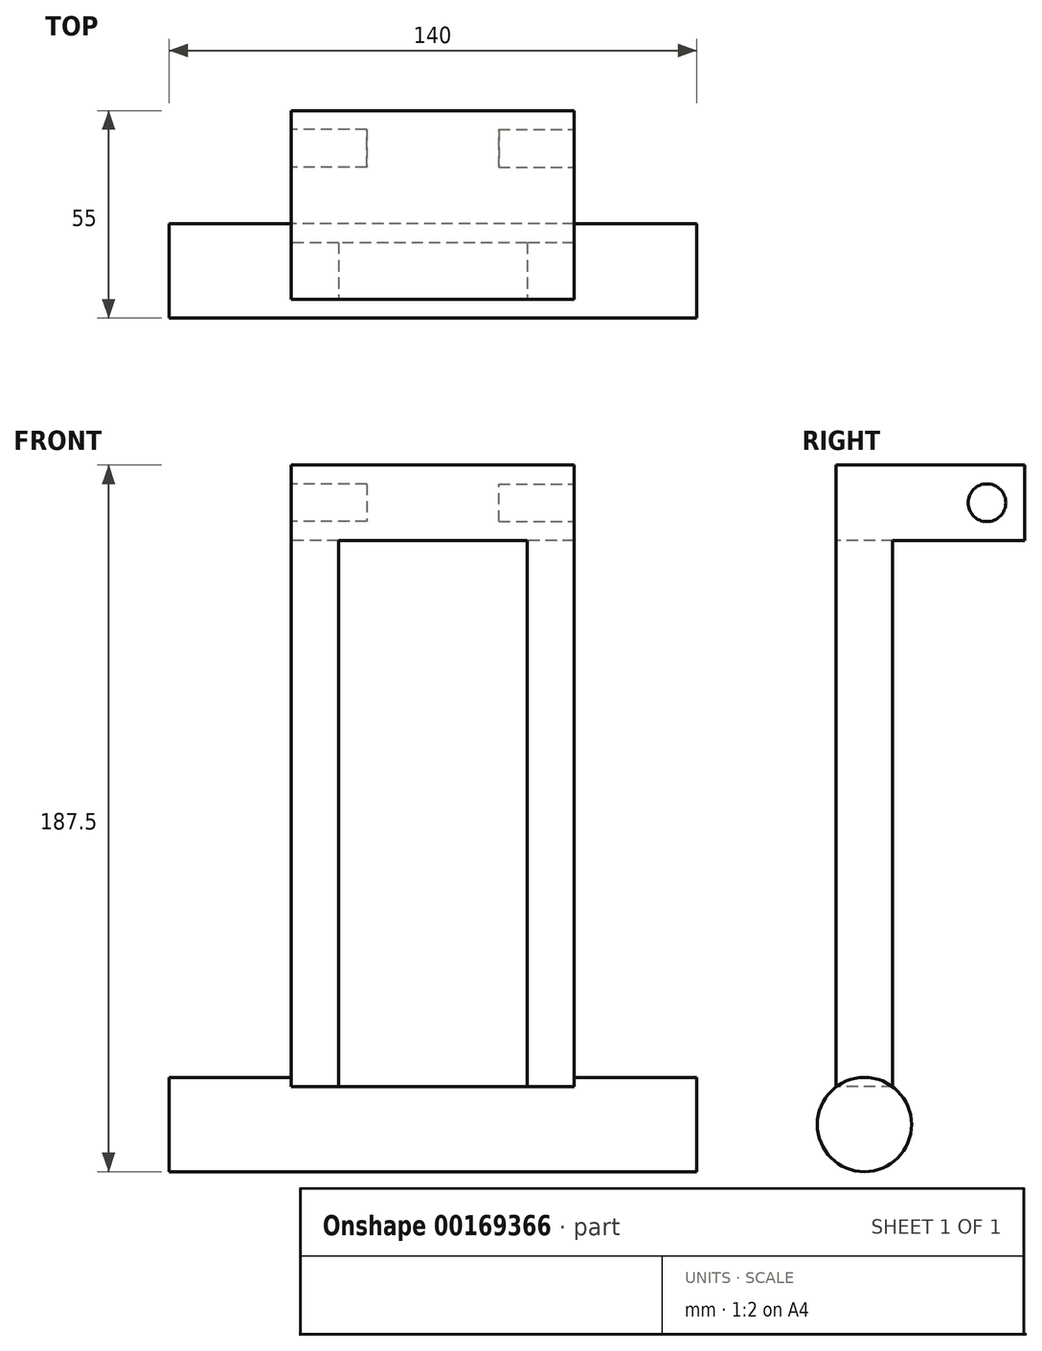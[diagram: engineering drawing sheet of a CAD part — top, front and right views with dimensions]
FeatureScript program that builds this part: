
annotation { "Feature Type Name" : "Feature", "Feature Type Description" : "" }
export const myFeature = defineFeature(function(context is Context, id is Id, definition is map)
    precondition{}
    {
        {
            var Q0;
            Q0=qCreatedBy(makeId("Right.planeOp"),FACE);
            var sketch = newSketch(context, id + "F0", { "sketchPlane" : qUnion([Q0])});
            skCircle(sketch, "E0", {"center": v(0, 0) * mm, "radius": 12.5 * mm});
            skSolve(sketch);
        }
        {
            var Q0;
            Q0=makeQuery(id+"F0.imprint","IMPRINT",FACE,{"disambiguationData":[TD([[makeQuery(id+"F0.imprint","IMPRINT",EDGE,{"derivedFrom":sQuery(id+"F0.wireOp",EDGE,"E0")}),1.0]])]});
            extrude(context, id + "F1", {"entities" : qUnion([Q0]), "endBound" : BoundingType.SYMMETRIC, "depth" : 140 * mm});
        }
        {
            var Q0;
            Q0=qCreatedBy(makeId("Top.planeOp"),FACE);
            var sketch = newSketch(context, id + "F2", { "sketchPlane" : qUnion([Q0])});
            skLineSegment(sketch, "E1.bottom", {"start": v(37.5, 7.5) * mm, "end": v(-37.5, 7.5) * mm});
            skLineSegment(sketch, "E1.top", {"start": v(37.5, -7.5) * mm, "end": v(-37.5, -7.5) * mm});
            skLineSegment(sketch, "E1.left", {"start": v(37.5, 7.5) * mm, "end": v(37.5, -7.5) * mm});
            skLineSegment(sketch, "E1.right", {"start": v(-37.5, 7.5) * mm, "end": v(-37.5, -7.5) * mm});
            skPoint(sketch, "E1.middle", {"position": v(0, 0) * mm});
            skSolve(sketch);
        }
        {
            var Q0;
            Q0=qSketchRegion(id+"F2",true);
            extrude(context, id + "F3", {"entities" : qUnion([Q0]), "operationType" : NewBodyOperationType.ADD, "depth" : 175 * mm});
        }
        {
            var Q0;
            Q0=makeQuery(id+"F3.opExtrude","SWEPT_FACE",FACE,{"disambiguationData":[OSD([sQuery(id+"F2.wireOp",EDGE,"E1.top")])]});
            var sketch = newSketch(context, id + "F4", { "sketchPlane" : qUnion([Q0])});
            skLineSegment(sketch, "E2.bottom", {"start": v(0, 10) * mm, "end": v(25, 10) * mm});
            skLineSegment(sketch, "E2.top", {"start": v(0, 155) * mm, "end": v(25, 155) * mm});
            skLineSegment(sketch, "E2.left", {"start": v(0, 10) * mm, "end": v(0, 155) * mm});
            skLineSegment(sketch, "E2.right", {"start": v(25, 10) * mm, "end": v(25, 155) * mm});
            skLineSegment(sketch, "E3.MirrorCS", {"start": v(0, 155) * mm, "end": v(-25, 155) * mm});
            skLineSegment(sketch, "E4.MirrorCS", {"start": v(-25, 10) * mm, "end": v(-25, 155) * mm});
            skLineSegment(sketch, "E5.MirrorCS", {"start": v(0, 10) * mm, "end": v(-25, 10) * mm});
            skSolve(sketch);
        }
        {
            var Q0;
            Q0=makeQuery(id+"F4.imprint","IMPRINT",FACE,{"disambiguationData":[TD([[makeQuery(id+"F4.imprint","IMPRINT",EDGE,{"derivedFrom":sQuery(id+"F4.wireOp",EDGE,"E2.left")}),1.0]])]});
            var Q1;
            Q1=makeQuery(id+"F4.imprint","IMPRINT",FACE,{"disambiguationData":[TD([[makeQuery(id+"F4.imprint","IMPRINT",EDGE,{"derivedFrom":sQuery(id+"F4.wireOp",EDGE,"E2.bottom")}),-1.0]])]});
            extrude(context, id + "F5", {"entities" : qUnion([Q0, Q1]), "operationType" : NewBodyOperationType.REMOVE, "oppositeDirection" : true, "depth" : 500 * mm});
        }
        {
            var Q0;
            Q0=makeQuery(id+"F3.opExtrude","SWEPT_FACE",FACE,{"disambiguationData":[OSD([sQuery(id+"F2.wireOp",EDGE,"E1.top")])]});
            var sketch = newSketch(context, id + "F6", { "sketchPlane" : qUnion([Q0])});
            skPoint(sketch, "E6.oppositeSnap0", {"position": v(0, 155) * mm});
            skLineSegment(sketch, "E6.bottom", {"start": v(-37.5, 175) * mm, "end": v(37.5, 175) * mm});
            skLineSegment(sketch, "E6.top", {"start": v(-37.5, 155) * mm, "end": v(37.5, 155) * mm});
            skLineSegment(sketch, "E6.left", {"start": v(-37.5, 175) * mm, "end": v(-37.5, 155) * mm});
            skLineSegment(sketch, "E6.right", {"start": v(37.5, 175) * mm, "end": v(37.5, 155) * mm});
            skSolve(sketch);
        }
        {
            var Q0;
            Q0=qSketchRegion(id+"F6",true);
            extrude(context, id + "F7", {"entities" : qUnion([Q0]), "operationType" : NewBodyOperationType.ADD, "oppositeDirection" : true, "depth" : 50 * mm});
        }
        {
            var Q0;
            Q0=makeQuery(id+"F7.boolean.opBoolean","MERGE",FACE,{"derivedFrom":[makeQuery(id+"F3.opExtrude","SWEPT_FACE",FACE,{"disambiguationData":[OSD([sQuery(id+"F2.wireOp",EDGE,"E1.right")])]}),makeQuery(id+"F7.opExtrude","SWEPT_FACE",FACE,{"disambiguationData":[OSD([sQuery(id+"F6.wireOp",EDGE,"E6.left")])]})]});
            var sketch = newSketch(context, id + "F8", { "sketchPlane" : qUnion([Q0])});
            skPoint(sketch, "E7", {"position": v(-42.5, 165) * mm});
            skCircle(sketch, "E8", {"center": v(-32.5, 165) * mm, "radius": 5 * mm});
            skSolve(sketch);
        }
        {
            var Q0;
            Q0=makeQuery(id+"F8.imprint","IMPRINT",FACE,{"disambiguationData":[TD([[makeQuery(id+"F8.imprint","IMPRINT",EDGE,{"derivedFrom":sQuery(id+"F8.wireOp",EDGE,"E8")}),1.0]])]});
            extrude(context, id + "F9", {"entities" : qUnion([Q0]), "operationType" : NewBodyOperationType.REMOVE, "oppositeDirection" : true, "depth" : 20 * mm});
        }
        {
            var Q0;
            Q0=makeQuery(id+"F7.boolean.opBoolean","MERGE",FACE,{"derivedFrom":[makeQuery(id+"F3.opExtrude","SWEPT_FACE",FACE,{"disambiguationData":[OSD([sQuery(id+"F2.wireOp",EDGE,"E1.left")])]}),makeQuery(id+"F7.opExtrude","SWEPT_FACE",FACE,{"disambiguationData":[OSD([sQuery(id+"F6.wireOp",EDGE,"E6.right")])]})]});
            var sketch = newSketch(context, id + "F10", { "sketchPlane" : qUnion([Q0])});
            skPoint(sketch, "E9", {"position": v(42.5, 165) * mm});
            skCircle(sketch, "E10", {"center": v(32.5, 165) * mm, "radius": 5 * mm});
            skSolve(sketch);
        }
        {
            var Q0;
            Q0=qSketchRegion(id+"F10",true);
            extrude(context, id + "F11", {"entities" : qUnion([Q0]), "operationType" : NewBodyOperationType.REMOVE, "oppositeDirection" : true, "depth" : 20 * mm});
        }
    });
